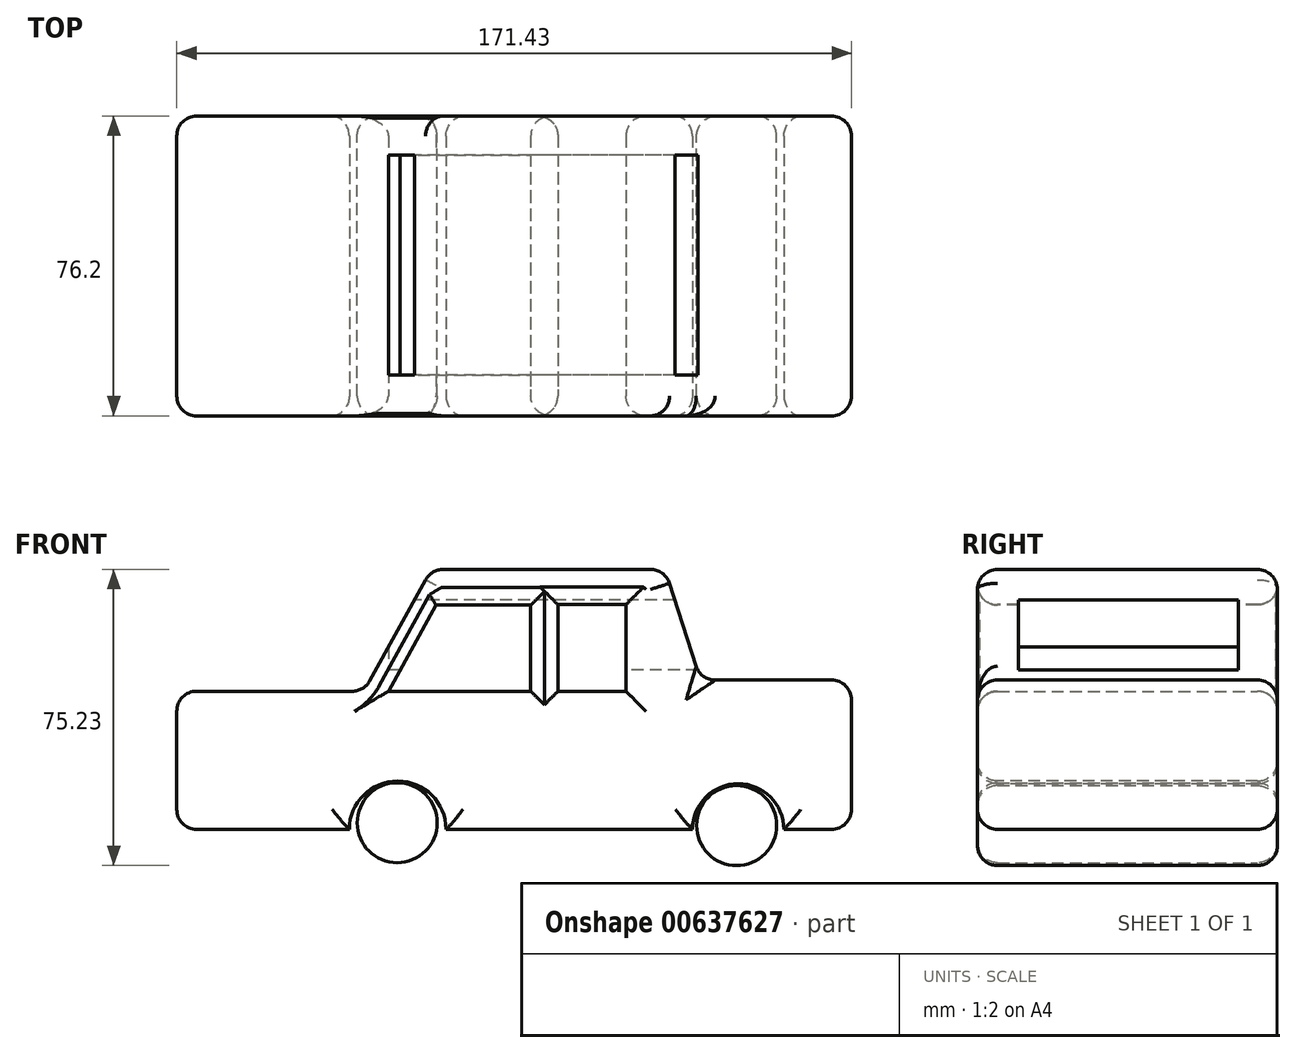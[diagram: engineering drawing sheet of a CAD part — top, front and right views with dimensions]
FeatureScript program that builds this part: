
annotation { "Feature Type Name" : "Feature", "Feature Type Description" : "" }
export const myFeature = defineFeature(function(context is Context, id is Id, definition is map)
    precondition{}
    {
        {
            var Q0;
            Q0=qCreatedBy(makeId("Front.planeOp"),FACE);
            var sketch = newSketch(context, id + "F0", { "sketchPlane" : qUnion([Q0])});
            skLineSegment(sketch, "E0", {"start": v(-54.36, 0) * mm, "end": v(-6.2, 0) * mm});
            skLineSegment(sketch, "E1", {"start": v(-6.2, 0) * mm, "end": v(10.91, 30.96) * mm});
            skLineSegment(sketch, "E2", {"start": v(10.91, 30.96) * mm, "end": v(70.28, 30.96) * mm});
            skLineSegment(sketch, "E3", {"start": v(70.28, 30.96) * mm, "end": v(79.32, 2.85) * mm});
            skLineSegment(sketch, "E4", {"start": v(79.32, 2.85) * mm, "end": v(117.66, 2.85) * mm});
            skLineSegment(sketch, "E5", {"start": v(117.66, 2.85) * mm, "end": v(117.66, -35.1) * mm});
            skLineSegment(sketch, "E6", {"start": v(117.66, -35.1) * mm, "end": v(76.96, -35.1) * mm});
            skLineSegment(sketch, "E7", {"start": v(76.96, -35.1) * mm, "end": v(-53.77, -35.1) * mm});
            skLineSegment(sketch, "E8", {"start": v(-53.77, -35.1) * mm, "end": v(-53.77, 0) * mm});
            skSolve(sketch);
        }
        {
            var Q0;
            {var subQ0=sQuery(id+"F0.wireOp",EDGE,"E1");Q0=makeQuery(id+"F0.imprint","IMPRINT",FACE,{"disambiguationData":[TD([[makeQuery(id+"F0.imprint","IMPRINT",EDGE,{"derivedFrom":subQ0}),-1.0]])]});}
            extrude(context, id + "F1", {"entities" : qUnion([Q0]), "depth" : 76.2 * mm, "offsetDistance" : 25.4 * mm});
        }
        {
            var Q0;
            Q0=makeQuery(id+"F1.opExtrude","CAP_FACE",FACE,{"disambiguationData":[OSD([sQuery(id+"F0.wireOp",EDGE,"E0"),sQuery(id+"F0.wireOp",EDGE,"E1"),sQuery(id+"F0.wireOp",EDGE,"E2"),sQuery(id+"F0.wireOp",EDGE,"E3"),sQuery(id+"F0.wireOp",EDGE,"E4"),sQuery(id+"F0.wireOp",EDGE,"E5"),sQuery(id+"F0.wireOp",EDGE,"E6"),sQuery(id+"F0.wireOp",EDGE,"E7"),sQuery(id+"F0.wireOp",EDGE,"E8")])],"isStart":false});
            var sketch = newSketch(context, id + "F2", { "sketchPlane" : qUnion([Q0])});
            skCircle(sketch, "E9", {"center": v(2.35, -35.1) * mm, "radius": 12.28 * mm});
            skSolve(sketch);
        }
        {
            var Q0;
            Q0 = qSketchRegion(id + "F2", true);
            extrude(context, id + "F3", {"entities" : qUnion([Q0]), "operationType" : NewBodyOperationType.REMOVE, "oppositeDirection" : true, "depth" : 76.2 * mm, "offsetDistance" : 25.4 * mm});
        }
        {
            var Q0;
            Q0=makeQuery(id+"F1.opExtrude","CAP_FACE",FACE,{"disambiguationData":[OSD([sQuery(id+"F0.wireOp",EDGE,"E0"),sQuery(id+"F0.wireOp",EDGE,"E1"),sQuery(id+"F0.wireOp",EDGE,"E2"),sQuery(id+"F0.wireOp",EDGE,"E3"),sQuery(id+"F0.wireOp",EDGE,"E4"),sQuery(id+"F0.wireOp",EDGE,"E5"),sQuery(id+"F0.wireOp",EDGE,"E6"),sQuery(id+"F0.wireOp",EDGE,"E7"),sQuery(id+"F0.wireOp",EDGE,"E8")])],"isStart":false});
            var sketch = newSketch(context, id + "F4", { "sketchPlane" : qUnion([Q0])});
            skCircle(sketch, "E10", {"center": v(88.84, -35.1) * mm, "radius": 11.6 * mm});
            skSolve(sketch);
        }
        {
            var Q0;
            Q0 = qSketchRegion(id + "F4", true);
            extrude(context, id + "F5", {"entities" : qUnion([Q0]), "operationType" : NewBodyOperationType.REMOVE, "oppositeDirection" : true, "depth" : 76.2 * mm, "offsetDistance" : 25.4 * mm});
        }
        {
            var Q0;
            Q0=makeQuery(id+"F1.opExtrude","CAP_FACE",FACE,{"disambiguationData":[OSD([sQuery(id+"F0.wireOp",EDGE,"E0"),sQuery(id+"F0.wireOp",EDGE,"E1"),sQuery(id+"F0.wireOp",EDGE,"E2"),sQuery(id+"F0.wireOp",EDGE,"E3"),sQuery(id+"F0.wireOp",EDGE,"E4"),sQuery(id+"F0.wireOp",EDGE,"E5"),sQuery(id+"F0.wireOp",EDGE,"E6"),sQuery(id+"F0.wireOp",EDGE,"E7"),sQuery(id+"F0.wireOp",EDGE,"E8")])],"isStart":false});
            var sketch = newSketch(context, id + "F6", { "sketchPlane" : qUnion([Q0])});
            skLineSegment(sketch, "E11", {"start": v(0, 0) * mm, "end": v(12.09, 21.88) * mm});
            skLineSegment(sketch, "E12", {"start": v(12.09, 21.88) * mm, "end": v(29.28, 21.88) * mm});
            skLineSegment(sketch, "E13", {"start": v(29.28, 21.88) * mm, "end": v(36.16, 21.88) * mm});
            skLineSegment(sketch, "E14", {"start": v(36.16, 21.88) * mm, "end": v(36.16, 0) * mm});
            skLineSegment(sketch, "E15", {"start": v(36.16, 0) * mm, "end": v(0, 0) * mm});
            skSolve(sketch);
        }
        {
            var Q0;
            Q0 = qSketchRegion(id + "F6", true);
            extrude(context, id + "F7", {"entities" : qUnion([Q0]), "operationType" : NewBodyOperationType.REMOVE, "oppositeDirection" : true, "depth" : 76.2 * mm, "offsetDistance" : 25.4 * mm});
        }
        {
            var Q0;
            Q0=makeQuery(id+"F1.opExtrude","CAP_FACE",FACE,{"disambiguationData":[OSD([sQuery(id+"F0.wireOp",EDGE,"E0"),sQuery(id+"F0.wireOp",EDGE,"E1"),sQuery(id+"F0.wireOp",EDGE,"E2"),sQuery(id+"F0.wireOp",EDGE,"E3"),sQuery(id+"F0.wireOp",EDGE,"E4"),sQuery(id+"F0.wireOp",EDGE,"E5"),sQuery(id+"F0.wireOp",EDGE,"E6"),sQuery(id+"F0.wireOp",EDGE,"E7"),sQuery(id+"F0.wireOp",EDGE,"E8")])],"isStart":false});
            var sketch = newSketch(context, id + "F8", { "sketchPlane" : qUnion([Q0])});
            skLineSegment(sketch, "E16.bottom", {"start": v(60.33, 22) * mm, "end": v(43.06, 22) * mm});
            skLineSegment(sketch, "E16.top", {"start": v(60.33, 0) * mm, "end": v(43.06, 0) * mm});
            skLineSegment(sketch, "E16.left", {"start": v(60.33, 22) * mm, "end": v(60.33, 0) * mm});
            skLineSegment(sketch, "E16.right", {"start": v(43.06, 22) * mm, "end": v(43.06, 0) * mm});
            skSolve(sketch);
        }
        {
            var Q0;
            Q0 = qSketchRegion(id + "F8", true);
            extrude(context, id + "F9", {"entities" : qUnion([Q0]), "operationType" : NewBodyOperationType.REMOVE, "oppositeDirection" : true, "depth" : 76.2 * mm, "offsetDistance" : 25.4 * mm});
        }
        {
            var Q0;
            Q0=makeQuery(id+"F1.opExtrude","CAP_EDGE",EDGE,{"disambiguationData":[OSD([sQuery(id+"F0.wireOp",EDGE,"E2")])],"isStart":false});
            var Q1;
            Q1=makeQuery(id+"F1.opExtrude","SWEPT_FACE",FACE,{"disambiguationData":[OSD([sQuery(id+"F0.wireOp",EDGE,"E1")])]});
            var Q2;
            Q2=makeQuery(id+"F1.opExtrude","SWEPT_FACE",FACE,{"disambiguationData":[OSD([sQuery(id+"F0.wireOp",EDGE,"E8")])]});
            var Q3;
            Q3=makeQuery(id+"F1.opExtrude","CAP_EDGE",EDGE,{"disambiguationData":[OSD([sQuery(id+"F0.wireOp",EDGE,"E3")])],"isStart":false});
            var Q4;
            Q4=makeQuery(id+"F1.opExtrude","CAP_FACE",FACE,{"disambiguationData":[OSD([sQuery(id+"F0.wireOp",EDGE,"E0"),sQuery(id+"F0.wireOp",EDGE,"E1"),sQuery(id+"F0.wireOp",EDGE,"E2"),sQuery(id+"F0.wireOp",EDGE,"E3"),sQuery(id+"F0.wireOp",EDGE,"E4"),sQuery(id+"F0.wireOp",EDGE,"E5"),sQuery(id+"F0.wireOp",EDGE,"E6"),sQuery(id+"F0.wireOp",EDGE,"E7"),sQuery(id+"F0.wireOp",EDGE,"E8")])],"isStart":false});
            var Q5;
            Q5=makeQuery(id+"F1.opExtrude","CAP_EDGE",EDGE,{"disambiguationData":[OSD([sQuery(id+"F0.wireOp",EDGE,"E5")])],"isStart":false});
            fillet(context, id + "F10", {"entities" : qUnion([Q0, Q1, Q2, Q3, Q4, Q5]), "radius" : 5.08 * mm, "tangentPropagation" : true, "allowEdgeOverflow" : false});
        }
        {
            var Q0;
            Q0=makeQuery(id+"F1.opExtrude","SWEPT_EDGE",EDGE,{"disambiguationData":[OSD([sQuery(id+"F0.wireOp",EDGE,"E4"),sQuery(id+"F0.wireOp",EDGE,"E5")])]});
            var Q1;
            Q1=makeQuery(id+"F1.opExtrude","SWEPT_FACE",FACE,{"disambiguationData":[OSD([sQuery(id+"F0.wireOp",EDGE,"E3")])]});
            var Q2;
            Q2=makeQuery(id+"F1.opExtrude","SWEPT_FACE",FACE,{"disambiguationData":[OSD([sQuery(id+"F0.wireOp",EDGE,"E5")])]});
            var Q3;
            Q3=makeQuery(id+"F1.opExtrude","CAP_EDGE",EDGE,{"disambiguationData":[OSD([sQuery(id+"F0.wireOp",EDGE,"E2")])],"isStart":true});
            fillet(context, id + "F11", {"entities" : qUnion([Q0, Q1, Q2, Q3]), "radius" : 5.08 * mm, "tangentPropagation" : true, "allowEdgeOverflow" : false});
        }
        {
            var Q0;
            Q0=qCreatedBy(makeId("Front.planeOp"),FACE);
            var sketch = newSketch(context, id + "F12", { "sketchPlane" : qUnion([Q0])});
            skCircle(sketch, "E17", {"center": v(2.22, -33.41) * mm, "radius": 10.16 * mm});
            skSolve(sketch);
        }
        {
            var Q0;
            Q0 = qSketchRegion(id + "F12", true);
            extrude(context, id + "F13", {"entities" : qUnion([Q0]), "depth" : 76.2 * mm, "offsetDistance" : 25.4 * mm});
        }
        {
            var Q0;
            Q0=makeQuery(id+"F13.opExtrude","CAP_FACE",FACE,{"disambiguationData":[OSD([sQuery(id+"F12.wireOp",EDGE,"E17")])],"isStart":false});
            var Q1;
            Q1=makeQuery(id+"F13.opExtrude","CAP_FACE",FACE,{"disambiguationData":[OSD([sQuery(id+"F12.wireOp",EDGE,"E17")])],"isStart":true});
            fillet(context, id + "F14", {"entities" : qUnion([Q0, Q1]), "radius" : 5.08 * mm, "tangentPropagation" : true, "allowEdgeOverflow" : false});
        }
        {
            var Q0;
            Q0=qCreatedBy(makeId("Front.planeOp"),FACE);
            var sketch = newSketch(context, id + "F15", { "sketchPlane" : qUnion([Q0])});
            skCircle(sketch, "E18", {"center": v(88.45, -34.1) * mm, "radius": 10.16 * mm});
            skSolve(sketch);
        }
        {
            var Q0;
            Q0 = qSketchRegion(id + "F15", true);
            extrude(context, id + "F16", {"entities" : qUnion([Q0]), "depth" : 76.2 * mm, "offsetDistance" : 25.4 * mm});
        }
        {
            var Q0;
            Q0=makeQuery(id+"F16.opExtrude","CAP_FACE",FACE,{"disambiguationData":[OSD([sQuery(id+"F15.wireOp",EDGE,"E18")])],"isStart":false});
            fillet(context, id + "F17", {"entities" : qUnion([Q0]), "radius" : 5.08 * mm, "tangentPropagation" : true, "allowEdgeOverflow" : false});
        }
        {
            var Q0;
            Q0=makeQuery(id+"F16.opExtrude","CAP_FACE",FACE,{"disambiguationData":[OSD([sQuery(id+"F15.wireOp",EDGE,"E18")])],"isStart":true});
            fillet(context, id + "F18", {"entities" : qUnion([Q0]), "radius" : 5.08 * mm, "tangentPropagation" : true, "allowEdgeOverflow" : false});
        }
        {
            var Q0;
            Q0=makeQuery(id+"F1.opExtrude","CAP_FACE",FACE,{"disambiguationData":[OSD([sQuery(id+"F0.wireOp",EDGE,"E0"),sQuery(id+"F0.wireOp",EDGE,"E1"),sQuery(id+"F0.wireOp",EDGE,"E2"),sQuery(id+"F0.wireOp",EDGE,"E3"),sQuery(id+"F0.wireOp",EDGE,"E4"),sQuery(id+"F0.wireOp",EDGE,"E5"),sQuery(id+"F0.wireOp",EDGE,"E6"),sQuery(id+"F0.wireOp",EDGE,"E7"),sQuery(id+"F0.wireOp",EDGE,"E8")])],"isStart":true});
            fillet(context, id + "F19", {"entities" : qUnion([Q0]), "radius" : 5.08 * mm, "tangentPropagation" : true, "allowEdgeOverflow" : false});
        }
        {
            var Q0;
            Q0=qCreatedBy(makeId("Right.planeOp"),FACE);
            var sketch = newSketch(context, id + "F20", { "sketchPlane" : qUnion([Q0])});
            skLineSegment(sketch, "E19.bottom", {"start": v(-9.88, 23.19) * mm, "end": v(-65.76, 23.19) * mm});
            skLineSegment(sketch, "E19.top", {"start": v(-9.88, 5.4) * mm, "end": v(-65.76, 5.4) * mm});
            skLineSegment(sketch, "E19.left", {"start": v(-9.88, 23.19) * mm, "end": v(-9.88, 5.4) * mm});
            skLineSegment(sketch, "E19.right", {"start": v(-65.76, 23.19) * mm, "end": v(-65.76, 5.4) * mm});
            skSolve(sketch);
        }
        {
            var Q0;
            Q0 = qSketchRegion(id + "F20", true);
            extrude(context, id + "F21", {"entities" : qUnion([Q0]), "operationType" : NewBodyOperationType.REMOVE, "depth" : 130.56 * mm, "offsetDistance" : 25.4 * mm});
        }
    });
